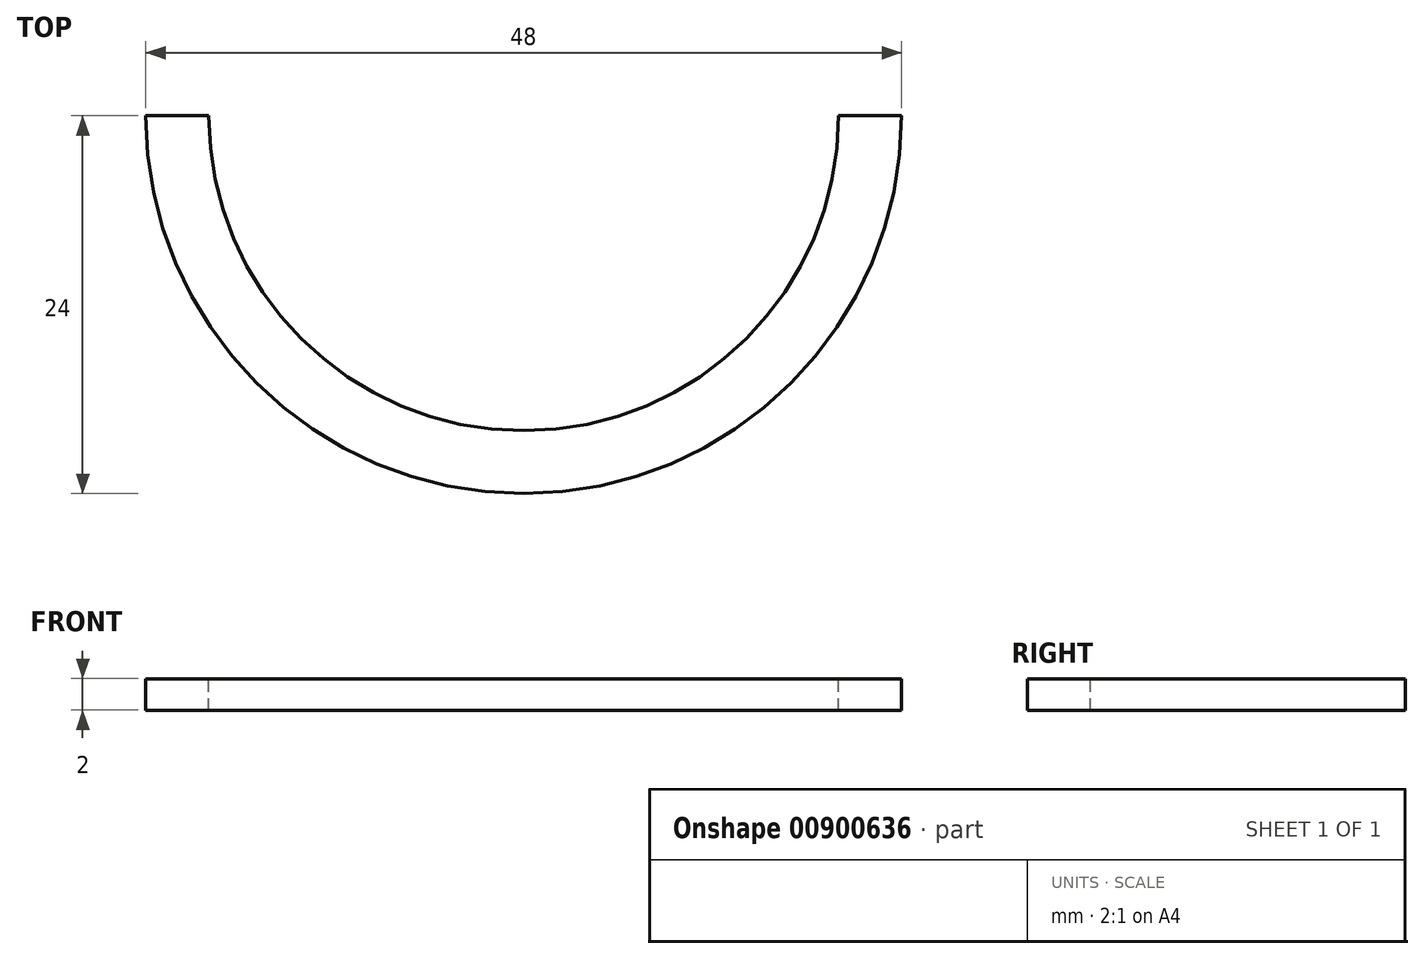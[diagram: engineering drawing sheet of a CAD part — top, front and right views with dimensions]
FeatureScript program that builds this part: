
annotation { "Feature Type Name" : "Feature", "Feature Type Description" : "" }
export const myFeature = defineFeature(function(context is Context, id is Id, definition is map)
    precondition{}
    {
        {
            var Q0;
            Q0=qCreatedBy(makeId("Front.planeOp"),FACE);
            var sketch = newSketch(context, id + "F0", { "sketchPlane" : qUnion([Q0])});
            skLineSegment(sketch, "E0.bottom", {"start": v(17.96, 0.89) * mm, "end": v(21.96, 0.89) * mm});
            skLineSegment(sketch, "E0.top", {"start": v(17.96, -1.11) * mm, "end": v(21.96, -1.11) * mm});
            skLineSegment(sketch, "E0.left", {"start": v(17.96, 0.89) * mm, "end": v(17.96, -1.11) * mm});
            skLineSegment(sketch, "E0.right", {"start": v(21.96, 0.89) * mm, "end": v(21.96, -1.11) * mm});
            skLineSegment(sketch, "E1", {"start": v(-2.04, 4.57) * mm, "end": v(-2.04, -3.2) * mm, "construction": true});
            skSolve(sketch);
        }
        {
            var Q0;
            Q0=makeQuery(id+"F0.imprint","IMPRINT",FACE,{"disambiguationData":[TD([[makeQuery(id+"F0.imprint","IMPRINT",EDGE,{"derivedFrom":sQuery(id+"F0.wireOp",EDGE,"E0.bottom")}),-1.0]])]});
            var Q1;
            Q1=sQuery(id+"F0.wireOp",EDGE,"E1");
            revolve(context, id + "F1", {"surfaceOperationType" : NewSurfaceOperationType.NEW, "entities" : qUnion([Q0]), "axis" : qUnion([Q1]), "revolveType" : RevolveType.FULL});
        }
        {
            var Q0;
            Q0=qCreatedBy(makeId("Front.planeOp"),FACE);
            var sketch = newSketch(context, id + "F2", { "sketchPlane" : qUnion([Q0])});
            skLineSegment(sketch, "E2.bottom", {"start": v(-45.18, 33.1) * mm, "end": v(36.67, 33.1) * mm});
            skLineSegment(sketch, "E2.top", {"start": v(-45.18, -34.03) * mm, "end": v(36.67, -34.03) * mm});
            skLineSegment(sketch, "E2.left", {"start": v(-45.18, 33.1) * mm, "end": v(-45.18, -34.03) * mm});
            skLineSegment(sketch, "E2.right", {"start": v(36.67, 33.1) * mm, "end": v(36.67, -34.03) * mm});
            skSolve(sketch);
        }
        {
            var Q0;
            Q0=makeQuery(id+"F2.imprint","IMPRINT",FACE,{"disambiguationData":[TD([[makeQuery(id+"F2.imprint","IMPRINT",EDGE,{"derivedFrom":sQuery(id+"F2.wireOp",EDGE,"E2.bottom")}),-1.0]])]});
            extrude(context, id + "F3", {"entities" : qUnion([Q0]), "operationType" : NewBodyOperationType.REMOVE, "endBound" : BoundingType.THROUGH_ALL, "oppositeDirection" : true, "depth" : 25 * mm, "offsetDistance" : 25 * mm});
        }
    });
